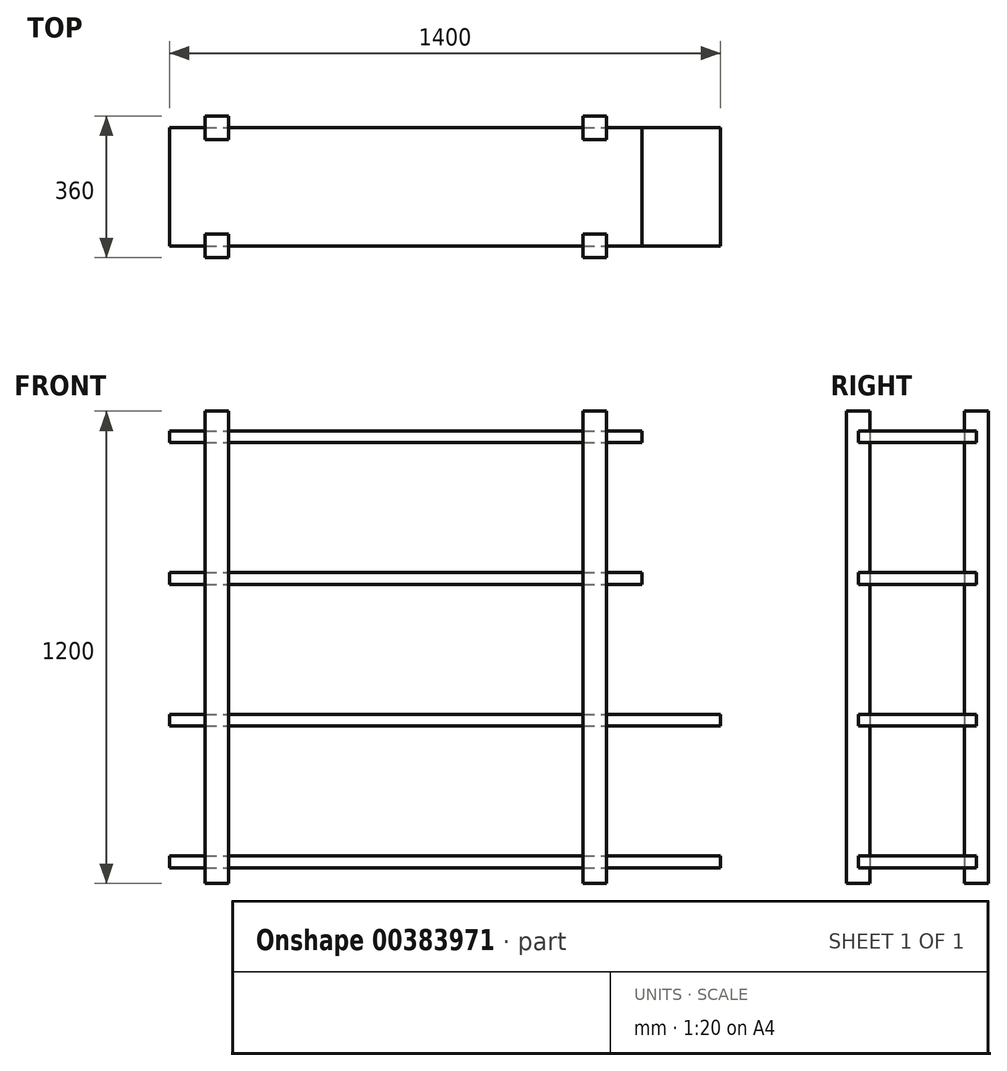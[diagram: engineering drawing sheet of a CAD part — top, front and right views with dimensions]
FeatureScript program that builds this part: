
annotation { "Feature Type Name" : "Feature", "Feature Type Description" : "" }
export const myFeature = defineFeature(function(context is Context, id is Id, definition is map)
    precondition{}
    {
        {
            var Q0;
            Q0=qCreatedBy(makeId("Front.planeOp"),FACE);
            var sketch = newSketch(context, id + "F0", { "sketchPlane" : qUnion([Q0])});
            skLineSegment(sketch, "E0.bottom", {"start": v(-700, 30) * mm, "end": v(700, 30) * mm});
            skLineSegment(sketch, "E0.top", {"start": v(-700, 0) * mm, "end": v(700, 0) * mm});
            skLineSegment(sketch, "E0.left", {"start": v(-700, 30) * mm, "end": v(-700, 0) * mm});
            skLineSegment(sketch, "E0.right", {"start": v(700, 30) * mm, "end": v(700, 0) * mm});
            skSolve(sketch);
        }
        {
            var Q0;
            Q0=qCreatedBy(makeId("Front.planeOp"),FACE);
            var sketch = newSketch(context, id + "F1", { "sketchPlane" : qUnion([Q0])});
            skLineSegment(sketch, "E1.bottom", {"start": v(-700, 390) * mm, "end": v(700, 390) * mm});
            skLineSegment(sketch, "E1.top", {"start": v(-700, 360) * mm, "end": v(700, 360) * mm});
            skLineSegment(sketch, "E1.left", {"start": v(-700, 390) * mm, "end": v(-700, 360) * mm});
            skLineSegment(sketch, "E1.right", {"start": v(700, 390) * mm, "end": v(700, 360) * mm});
            skSolve(sketch);
        }
        {
            var Q0;
            Q0=qCreatedBy(makeId("Front.planeOp"),FACE);
            var sketch = newSketch(context, id + "F2", { "sketchPlane" : qUnion([Q0])});
            skLineSegment(sketch, "E2.bottom", {"start": v(-700, 750) * mm, "end": v(500, 750) * mm});
            skLineSegment(sketch, "E2.top", {"start": v(-700, 720) * mm, "end": v(500, 720) * mm});
            skLineSegment(sketch, "E2.left", {"start": v(-700, 750) * mm, "end": v(-700, 720) * mm});
            skLineSegment(sketch, "E2.right", {"start": v(500, 750) * mm, "end": v(500, 720) * mm});
            skSolve(sketch);
        }
        {
            var Q0;
            Q0=qCreatedBy(makeId("Front.planeOp"),FACE);
            var sketch = newSketch(context, id + "F3", { "sketchPlane" : qUnion([Q0])});
            skLineSegment(sketch, "E3.bottom", {"start": v(-700, 1110) * mm, "end": v(500, 1110) * mm});
            skLineSegment(sketch, "E3.top", {"start": v(-700, 1080) * mm, "end": v(500, 1080) * mm});
            skLineSegment(sketch, "E3.left", {"start": v(-700, 1110) * mm, "end": v(-700, 1080) * mm});
            skLineSegment(sketch, "E3.right", {"start": v(500, 1110) * mm, "end": v(500, 1080) * mm});
            skSolve(sketch);
        }
        {
            var Q0;
            Q0=qCreatedBy(makeId("Front.planeOp"),FACE);
            var sketch = newSketch(context, id + "F4", { "sketchPlane" : qUnion([Q0])});
            skLineSegment(sketch, "E4.bottom", {"start": v(-610, 1160) * mm, "end": v(-550, 1160) * mm});
            skLineSegment(sketch, "E4.top", {"start": v(-610, -40) * mm, "end": v(-550, -40) * mm});
            skLineSegment(sketch, "E4.left", {"start": v(-610, 1160) * mm, "end": v(-610, -40) * mm});
            skLineSegment(sketch, "E4.right", {"start": v(-550, 1160) * mm, "end": v(-550, -40) * mm});
            skSolve(sketch);
        }
        {
            var Q0;
            Q0=qCreatedBy(makeId("Front.planeOp"),FACE);
            var sketch = newSketch(context, id + "F5", { "sketchPlane" : qUnion([Q0])});
            skLineSegment(sketch, "E5.bottom", {"start": v(350, 1160) * mm, "end": v(410, 1160) * mm});
            skLineSegment(sketch, "E5.top", {"start": v(350, -40) * mm, "end": v(410, -40) * mm});
            skLineSegment(sketch, "E5.left", {"start": v(350, 1160) * mm, "end": v(350, -40) * mm});
            skLineSegment(sketch, "E5.right", {"start": v(410, 1160) * mm, "end": v(410, -40) * mm});
            skSolve(sketch);
        }
        {
            var Q0;
            Q0 = qSketchRegion(id + "F0", true);
            extrude(context, id + "F6", {"entities" : qUnion([Q0]), "depth" : 300 * mm});
        }
        {
            var Q0;
            Q0 = qSketchRegion(id + "F1", true);
            var Q1;
            Q1=makeQuery(id+"F2.imprint","IMPRINT",FACE,{"disambiguationData":[TD([[makeQuery(id+"F2.imprint","IMPRINT",EDGE,{"derivedFrom":sQuery(id+"F2.wireOp",EDGE,"E2.bottom")}),-1.0]])]});
            var Q2;
            Q2=makeQuery(id+"F3.imprint","IMPRINT",FACE,{"disambiguationData":[TD([[makeQuery(id+"F3.imprint","IMPRINT",EDGE,{"derivedFrom":sQuery(id+"F3.wireOp",EDGE,"E3.bottom")}),-1.0]])]});
            extrude(context, id + "F7", {"entities" : qUnion([Q0, Q1, Q2]), "depth" : 300 * mm});
        }
        {
            var Q0;
            Q0=makeQuery(id+"F4.imprint","IMPRINT",FACE,{"disambiguationData":[TD([[makeQuery(id+"F4.imprint","IMPRINT",EDGE,{"derivedFrom":sQuery(id+"F4.wireOp",EDGE,"E4.bottom")}),-1.0]])]});
            extrude(context, id + "F8", {"entities" : qUnion([Q0]), "endBound" : BoundingType.SYMMETRIC, "depth" : 60 * mm});
        }
        {
            var Q0;
            Q0=qCreatedBy(makeId("Top.planeOp"),FACE);
            var sketch = newSketch(context, id + "F9", { "sketchPlane" : qUnion([Q0])});
            skLineSegment(sketch, "E6.bottom", {"start": v(-610, -270) * mm, "end": v(-550, -270) * mm});
            skLineSegment(sketch, "E6.top", {"start": v(-610, -330) * mm, "end": v(-550, -330) * mm});
            skLineSegment(sketch, "E6.left", {"start": v(-610, -270) * mm, "end": v(-610, -330) * mm});
            skLineSegment(sketch, "E6.right", {"start": v(-550, -270) * mm, "end": v(-550, -330) * mm});
            skSolve(sketch);
        }
        {
            var Q0;
            Q0 = qSketchRegion(id + "F9", true);
            extrude(context, id + "F10", {"entities" : qUnion([Q0]), "depth" : 1160 * mm, "hasSecondDirection" : true, "secondDirectionOppositeDirection" : true, "secondDirectionDepth" : 40 * mm});
        }
        {
            var Q0;
            Q0=qCreatedBy(makeId("Top.planeOp"),FACE);
            var sketch = newSketch(context, id + "F11", { "sketchPlane" : qUnion([Q0])});
            skLineSegment(sketch, "E7.bottom", {"start": v(350, -270) * mm, "end": v(410, -270) * mm});
            skLineSegment(sketch, "E7.top", {"start": v(350, -330) * mm, "end": v(410, -330) * mm});
            skLineSegment(sketch, "E7.left", {"start": v(350, -270) * mm, "end": v(350, -330) * mm});
            skLineSegment(sketch, "E7.right", {"start": v(410, -270) * mm, "end": v(410, -330) * mm});
            skSolve(sketch);
        }
        {
            var Q0;
            Q0 = qSketchRegion(id + "F11", true);
            extrude(context, id + "F12", {"entities" : qUnion([Q0]), "depth" : 1160 * mm, "hasSecondDirection" : true, "secondDirectionOppositeDirection" : true, "secondDirectionDepth" : 40 * mm});
        }
        {
            var Q0;
            Q0 = qSketchRegion(id + "F5", true);
            extrude(context, id + "F13", {"entities" : qUnion([Q0]), "endBound" : BoundingType.SYMMETRIC, "depth" : 60 * mm});
        }
    });
